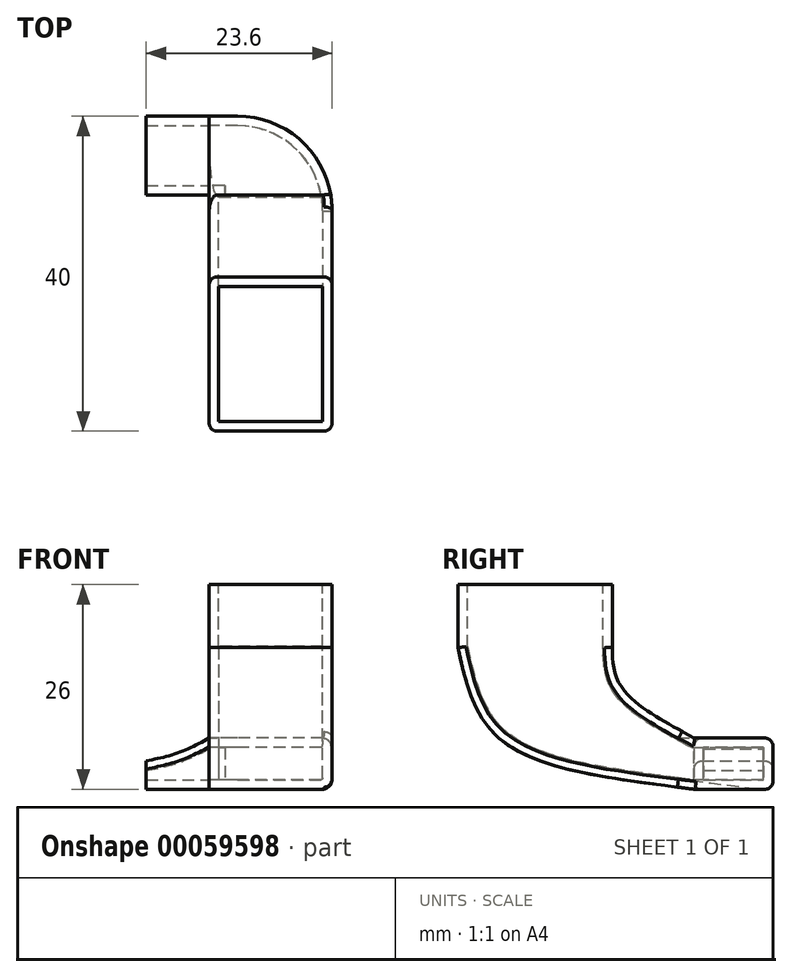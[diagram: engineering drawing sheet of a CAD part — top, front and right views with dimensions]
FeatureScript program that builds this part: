
annotation { "Feature Type Name" : "Feature", "Feature Type Description" : "" }
export const myFeature = defineFeature(function(context is Context, id is Id, definition is map)
    precondition{}
    {
        {
            var Q0;
            Q0=qCreatedBy(makeId("Right.planeOp"),FACE);
            var sketch = newSketch(context, id + "F0", { "sketchPlane" : qUnion([Q0])});
            skLineSegment(sketch, "E0.bottom", {"start": v(-14.31, 9.66) * mm, "end": v(25.69, 9.66) * mm, "construction": true});
            skLineSegment(sketch, "E0.top", {"start": v(-14.31, -16.34) * mm, "end": v(25.69, -16.34) * mm, "construction": true});
            skLineSegment(sketch, "E0.left", {"start": v(-14.31, 9.66) * mm, "end": v(-14.31, -16.34) * mm, "construction": true});
            skLineSegment(sketch, "E0.right", {"start": v(25.69, 9.66) * mm, "end": v(25.69, -16.34) * mm, "construction": true});
            skLineSegment(sketch, "E1", {"start": v(5.69, 9.66) * mm, "end": v(5.69, -16.34) * mm, "construction": true});
            skLineSegment(sketch, "E2", {"start": v(-14.31, -3.34) * mm, "end": v(25.69, -3.34) * mm, "construction": true});
            skLineSegment(sketch, "E3.bottom", {"start": v(-14.31, 9.66) * mm, "end": v(5.69, 9.66) * mm, "construction": true});
            skLineSegment(sketch, "E3.top", {"start": v(-14.31, -3.34) * mm, "end": v(5.69, -3.34) * mm, "construction": true});
            skLineSegment(sketch, "E3.left", {"start": v(-14.31, 9.66) * mm, "end": v(-14.31, -3.34) * mm, "construction": true});
            skLineSegment(sketch, "E3.right", {"start": v(5.69, 9.66) * mm, "end": v(5.69, -3.34) * mm, "construction": true});
            skLineSegment(sketch, "E4.bottom", {"start": v(5.69, -3.34) * mm, "end": v(25.69, -3.34) * mm, "construction": true});
            skLineSegment(sketch, "E4.top", {"start": v(5.69, -16.34) * mm, "end": v(25.69, -16.34) * mm, "construction": true});
            skLineSegment(sketch, "E4.left", {"start": v(5.69, -3.34) * mm, "end": v(5.69, -16.34) * mm, "construction": true});
            skLineSegment(sketch, "E4.right", {"start": v(25.69, -3.34) * mm, "end": v(25.69, -16.34) * mm, "construction": true});
            skLineSegment(sketch, "E5.bottom", {"start": v(25.69, 9.66) * mm, "end": v(5.69, 9.66) * mm, "construction": true});
            skLineSegment(sketch, "E5.top", {"start": v(25.69, -3.34) * mm, "end": v(5.69, -3.34) * mm, "construction": true});
            skLineSegment(sketch, "E5.left", {"start": v(25.69, 9.66) * mm, "end": v(25.69, -3.34) * mm, "construction": true});
            skLineSegment(sketch, "E6.bottom", {"start": v(-14.31, -16.34) * mm, "end": v(5.69, -16.34) * mm, "construction": true});
            skLineSegment(sketch, "E6.left", {"start": v(-14.31, -16.34) * mm, "end": v(-14.31, -3.34) * mm, "construction": true});
            skLineSegment(sketch, "E6.right", {"start": v(5.69, -16.34) * mm, "end": v(5.69, -3.34) * mm, "construction": true});
            skLineSegment(sketch, "E7.bottom", {"start": v(-4.31, 9.66) * mm, "end": v(5.69, 9.66) * mm, "construction": true});
            skLineSegment(sketch, "E7.top", {"start": v(-4.31, -3.34) * mm, "end": v(5.69, -3.34) * mm, "construction": true});
            skLineSegment(sketch, "E7.left", {"start": v(-4.31, 9.66) * mm, "end": v(-4.31, -3.34) * mm, "construction": true});
            skLineSegment(sketch, "E8.bottom", {"start": v(15.69, 9.66) * mm, "end": v(25.69, 9.66) * mm, "construction": true});
            skLineSegment(sketch, "E8.top", {"start": v(15.69, -3.34) * mm, "end": v(25.69, -3.34) * mm, "construction": true});
            skLineSegment(sketch, "E8.left", {"start": v(15.69, 9.66) * mm, "end": v(15.69, -3.34) * mm, "construction": true});
            skLineSegment(sketch, "E9.bottom", {"start": v(25.69, -16.34) * mm, "end": v(15.69, -16.34) * mm, "construction": true});
            skLineSegment(sketch, "E9.top", {"start": v(25.69, -3.34) * mm, "end": v(15.69, -3.34) * mm, "construction": true});
            skLineSegment(sketch, "E9.left", {"start": v(25.69, -16.34) * mm, "end": v(25.69, -3.34) * mm, "construction": true});
            skLineSegment(sketch, "E9.right", {"start": v(15.69, -16.34) * mm, "end": v(15.69, -3.34) * mm, "construction": true});
            skLineSegment(sketch, "E10.bottom", {"start": v(-4.31, -16.34) * mm, "end": v(5.69, -16.34) * mm, "construction": true});
            skLineSegment(sketch, "E10.left", {"start": v(-4.31, -16.34) * mm, "end": v(-4.31, -3.34) * mm, "construction": true});
            skLineSegment(sketch, "E11.bottom", {"start": v(-14.31, 9.66) * mm, "end": v(-4.31, 9.66) * mm, "construction": true});
            skLineSegment(sketch, "E11.top", {"start": v(-14.31, -3.34) * mm, "end": v(-4.31, -3.34) * mm, "construction": true});
            skLineSegment(sketch, "E12.top", {"start": v(-14.31, -16.34) * mm, "end": v(-4.31, -16.34) * mm, "construction": true});
            skLineSegment(sketch, "E12.left", {"start": v(-14.31, -3.34) * mm, "end": v(-14.31, -16.34) * mm, "construction": true});
            skLineSegment(sketch, "E12.right", {"start": v(-4.31, -3.34) * mm, "end": v(-4.31, -16.34) * mm, "construction": true});
            skLineSegment(sketch, "E13.bottom", {"start": v(5.69, 9.66) * mm, "end": v(15.69, 9.66) * mm, "construction": true});
            skLineSegment(sketch, "E13.top", {"start": v(5.69, -3.34) * mm, "end": v(15.69, -3.34) * mm, "construction": true});
            skLineSegment(sketch, "E14.bottom", {"start": v(-14.31, 3.16) * mm, "end": v(25.69, 3.16) * mm, "construction": true});
            skLineSegment(sketch, "E14.left", {"start": v(-14.31, 3.16) * mm, "end": v(-14.31, -3.34) * mm, "construction": true});
            skLineSegment(sketch, "E14.right", {"start": v(25.69, 3.16) * mm, "end": v(25.69, -3.34) * mm, "construction": true});
            skLineSegment(sketch, "E15.top", {"start": v(-14.31, -9.84) * mm, "end": v(25.69, -9.84) * mm, "construction": true});
            skLineSegment(sketch, "E15.left", {"start": v(-14.31, -3.34) * mm, "end": v(-14.31, -9.84) * mm, "construction": true});
            skLineSegment(sketch, "E15.right", {"start": v(25.69, -3.34) * mm, "end": v(25.69, -9.84) * mm, "construction": true});
            skLineSegment(sketch, "E16.bottom", {"start": v(-14.31, 9.66) * mm, "end": v(5.29, 9.66) * mm});
            skLineSegment(sketch, "E16.top", {"start": v(-14.31, 1.66) * mm, "end": v(5.29, 1.66) * mm, "construction": true});
            skLineSegment(sketch, "E16.left", {"start": v(-14.31, 9.66) * mm, "end": v(-14.31, 1.66) * mm});
            skLineSegment(sketch, "E16.right", {"start": v(5.29, 9.66) * mm, "end": v(5.29, 1.66) * mm});
            skLineSegment(sketch, "E17.bottom", {"start": v(25.69, -16.34) * mm, "end": v(15.69, -16.34) * mm});
            skLineSegment(sketch, "E17.top", {"start": v(25.69, -8.34) * mm, "end": v(15.69, -8.34) * mm, "construction": true});
            skLineSegment(sketch, "E17.left", {"start": v(25.69, -16.34) * mm, "end": v(25.69, -8.34) * mm});
            skLineSegment(sketch, "E17.right", {"start": v(15.69, -16.34) * mm, "end": v(15.69, -8.34) * mm, "construction": true});
            skFitSpline(sketch, "E18", {"points": [v(-14.31, 1.66) * mm, v(-9.11, -9.84) * mm, v(15.69, -16.34) * mm], "startDerivative": vector(6.77, -30.78) * mm, "endDerivative": vector(54.04, -6.84) * mm});
            skFitSpline(sketch, "E19", {"points": [v(5.29, 1.66) * mm, v(6.44, -3.34) * mm, v(15.69, -9.84) * mm], "startDerivative": vector(0.34, -12.73) * mm, "endDerivative": vector(19.24, -10.42) * mm});
            skLineSegment(sketch, "E20", {"start": v(15.69, -9.84) * mm, "end": v(25.69, -9.84) * mm});
            skSolve(sketch);
        }
        {
            var Q0;
            Q0=makeQuery(id+"F0.imprint","IMPRINT",FACE,{"disambiguationData":[TD([[makeQuery(id+"F0.imprint","IMPRINT",EDGE,{"derivedFrom":sQuery(id+"F0.wireOp",EDGE,"E16.bottom")}),-1.0]])]});
            var Q1;
            {var subQ4=sQuery(id+"F0.wireOp",EDGE,"E16.top");Q1=makeQuery(id+"F0.imprint","IMPRINT",FACE,{"disambiguationData":[TD([[makeQuery(id+"F0.imprint","IMPRINT",EDGE,{"derivedFrom":subQ4}),-1.0]])]});}
            var Q2;
            {var subQ0=sQuery(id+"F0.wireOp",EDGE,"E17.top");Q2=makeQuery(id+"F0.imprint","IMPRINT",FACE,{"disambiguationData":[TD([[makeQuery(id+"F0.imprint","IMPRINT",EDGE,{"derivedFrom":subQ0}),1.0]])]});}
            extrude(context, id + "F1", {"entities" : qUnion([Q0, Q1, Q2]), "depth" : 15.6 * mm});
        }
        {
            var Q0;
            Q0=makeQuery(id+"F1.opExtrude","SWEPT_FACE",FACE,{"disambiguationData":[OSD([sQuery(id+"F0.wireOp",EDGE,"E17.left")])]});
            cPlane(context, id + "F2", {"entities" : qUnion([Q0]), "cplaneType" : CPlaneType.OFFSET, "offset" : 0 * mm, "width" : 150 * mm, "height" : 150 * mm});
        }
        {
            var Q0;
            Q0=qCreatedBy(id+"F2.planeOp",FACE);
            var sketch = newSketch(context, id + "F3", { "sketchPlane" : qUnion([Q0])});
            skLineSegment(sketch, "E21", {"start": v(-15.6, -12.94) * mm, "end": v(-15.6, -12.74) * mm});
            skLineSegment(sketch, "E22", {"start": v(-15.6, -16.34) * mm, "end": v(-15.6, -9.34) * mm});
            skLineSegment(sketch, "E23.bottom", {"start": v(-15.6, -16.34) * mm, "end": v(-23.6, -16.34) * mm, "construction": true});
            skLineSegment(sketch, "E23.top", {"start": v(-15.6, -9.34) * mm, "end": v(-23.6, -9.34) * mm, "construction": true});
            skLineSegment(sketch, "E23.left", {"start": v(-15.6, -16.34) * mm, "end": v(-15.6, -9.34) * mm, "construction": true});
            skLineSegment(sketch, "E23.right", {"start": v(-23.6, -16.34) * mm, "end": v(-23.6, -9.34) * mm, "construction": true});
            skLineSegment(sketch, "E24.bottom", {"start": v(-13.35, -9.34) * mm, "end": v(-19.6, -9.34) * mm, "construction": true});
            skLineSegment(sketch, "E24.top", {"start": v(-13.35, -16.34) * mm, "end": v(-19.6, -16.34) * mm, "construction": true});
            skLineSegment(sketch, "E24.left", {"start": v(-13.35, -9.34) * mm, "end": v(-13.35, -16.34) * mm, "construction": true});
            skLineSegment(sketch, "E24.right", {"start": v(-19.6, -9.34) * mm, "end": v(-19.6, -16.34) * mm, "construction": true});
            skLineSegment(sketch, "E25.bottom", {"start": v(-19.6, -16.34) * mm, "end": v(-23.6, -16.34) * mm, "construction": true});
            skLineSegment(sketch, "E25.top", {"start": v(-19.6, -9.34) * mm, "end": v(-23.6, -9.34) * mm, "construction": true});
            skLineSegment(sketch, "E25.left", {"start": v(-19.6, -16.34) * mm, "end": v(-19.6, -9.34) * mm, "construction": true});
            skLineSegment(sketch, "E26.bottom", {"start": v(-23.6, -12.84) * mm, "end": v(-19.6, -12.84) * mm, "construction": true});
            skLineSegment(sketch, "E26.top", {"start": v(-23.6, -9.34) * mm, "end": v(-19.6, -9.34) * mm, "construction": true});
            skLineSegment(sketch, "E26.left", {"start": v(-23.6, -12.84) * mm, "end": v(-23.6, -9.34) * mm, "construction": true});
            skLineSegment(sketch, "E26.right", {"start": v(-19.6, -12.84) * mm, "end": v(-19.6, -9.34) * mm, "construction": true});
            skLineSegment(sketch, "E27.bottom", {"start": v(-13.35, -9.34) * mm, "end": v(-23.6, -9.34) * mm, "construction": true});
            skLineSegment(sketch, "E27.top", {"start": v(-13.35, -12.84) * mm, "end": v(-23.6, -12.84) * mm, "construction": true});
            skLineSegment(sketch, "E27.left", {"start": v(-13.35, -9.34) * mm, "end": v(-13.35, -12.84) * mm, "construction": true});
            skLineSegment(sketch, "E27.right", {"start": v(-23.6, -9.34) * mm, "end": v(-23.6, -12.84) * mm, "construction": true});
            skLineSegment(sketch, "E28.bottom", {"start": v(-19.6, -12.84) * mm, "end": v(-15.6, -12.84) * mm, "construction": true});
            skLineSegment(sketch, "E28.top", {"start": v(-19.6, -16.34) * mm, "end": v(-15.6, -16.34) * mm, "construction": true});
            skLineSegment(sketch, "E28.left", {"start": v(-19.6, -12.84) * mm, "end": v(-19.6, -16.34) * mm, "construction": true});
            skLineSegment(sketch, "E28.right", {"start": v(-15.6, -12.84) * mm, "end": v(-15.6, -16.34) * mm, "construction": true});
            skLineSegment(sketch, "E29.bottom", {"start": v(-23.6, -9.34) * mm, "end": v(-21.6, -9.34) * mm, "construction": true});
            skLineSegment(sketch, "E29.top", {"start": v(-23.6, -12.84) * mm, "end": v(-21.6, -12.84) * mm, "construction": true});
            skLineSegment(sketch, "E29.right", {"start": v(-21.6, -9.34) * mm, "end": v(-21.6, -12.84) * mm, "construction": true});
            skLineSegment(sketch, "E30.bottom", {"start": v(-19.6, -12.84) * mm, "end": v(-21.6, -12.84) * mm, "construction": true});
            skLineSegment(sketch, "E30.top", {"start": v(-19.6, -16.34) * mm, "end": v(-21.6, -16.34) * mm, "construction": true});
            skLineSegment(sketch, "E30.right", {"start": v(-21.6, -12.84) * mm, "end": v(-21.6, -16.34) * mm, "construction": true});
            skLineSegment(sketch, "E31.bottom", {"start": v(-19.6, -12.84) * mm, "end": v(-17.6, -12.84) * mm, "construction": true});
            skLineSegment(sketch, "E31.top", {"start": v(-19.6, -16.34) * mm, "end": v(-17.6, -16.34) * mm, "construction": true});
            skLineSegment(sketch, "E31.right", {"start": v(-17.6, -12.84) * mm, "end": v(-17.6, -16.34) * mm, "construction": true});
            skLineSegment(sketch, "E32.bottom", {"start": v(-13.35, -9.34) * mm, "end": v(-17.6, -9.34) * mm, "construction": true});
            skLineSegment(sketch, "E32.top", {"start": v(-13.35, -12.84) * mm, "end": v(-17.6, -12.84) * mm, "construction": true});
            skLineSegment(sketch, "E32.right", {"start": v(-17.6, -9.34) * mm, "end": v(-17.6, -12.84) * mm, "construction": true});
            skLineSegment(sketch, "E33.bottom", {"start": v(-24.97, -16.34) * mm, "end": v(-23.6, -16.34) * mm});
            skLineSegment(sketch, "E33.top", {"start": v(-24.97, -12.74) * mm, "end": v(-23.6, -12.74) * mm, "construction": true});
            skLineSegment(sketch, "E33.left", {"start": v(-23.6, -16.34) * mm, "end": v(-23.6, -12.74) * mm});
            skLineSegment(sketch, "E33.right", {"start": v(-24.97, -16.34) * mm, "end": v(-24.97, -12.74) * mm, "construction": true});
            skLineSegment(sketch, "E34", {"start": v(-15.6, -16.34) * mm, "end": v(-23.6, -16.34) * mm});
            skLineSegment(sketch, "E35", {"start": v(-15.6, -9.84) * mm, "end": v(0, -9.84) * mm});
            skLineSegment(sketch, "E36", {"start": v(-15.6, -16.34) * mm, "end": v(0, -16.34) * mm});
            skLineSegment(sketch, "E37", {"start": v(0, -16.34) * mm, "end": v(0, -9.34) * mm});
            skLineSegment(sketch, "E38", {"start": v(-7.8, -9.84) * mm, "end": v(-7.8, -16.34) * mm, "construction": true});
            skLineSegment(sketch, "E39.MirrorCS", {"start": v(8, -9.34) * mm, "end": v(8, -12.84) * mm, "construction": true});
            skLineSegment(sketch, "E40.MirrorCS", {"start": v(4, -12.84) * mm, "end": v(4, -9.34) * mm, "construction": true});
            skLineSegment(sketch, "E41.MirrorCS", {"start": v(8, -16.34) * mm, "end": v(8, -9.34) * mm, "construction": true});
            skLineSegment(sketch, "E42.MirrorCS", {"start": v(4, -12.84) * mm, "end": v(4, -16.34) * mm, "construction": true});
            skLineSegment(sketch, "E43.MirrorCS", {"start": v(4, -12.84) * mm, "end": v(6, -12.84) * mm, "construction": true});
            skLineSegment(sketch, "E44.MirrorCS", {"start": v(4, -16.34) * mm, "end": v(6, -16.34) * mm, "construction": true});
            skLineSegment(sketch, "E45.MirrorCS", {"start": v(8, -9.34) * mm, "end": v(4, -9.34) * mm, "construction": true});
            skLineSegment(sketch, "E46.MirrorCS", {"start": v(4, -9.34) * mm, "end": v(4, -16.34) * mm, "construction": true});
            skLineSegment(sketch, "E47.MirrorCS", {"start": v(9.37, -12.74) * mm, "end": v(8, -12.74) * mm, "construction": true});
            skLineSegment(sketch, "E48.MirrorCS", {"start": v(8, -12.84) * mm, "end": v(6, -12.84) * mm, "construction": true});
            skLineSegment(sketch, "E49.MirrorCS", {"start": v(4, -16.34) * mm, "end": v(4, -9.34) * mm, "construction": true});
            skLineSegment(sketch, "E50.MirrorCS", {"start": v(2, -9.34) * mm, "end": v(2, -12.84) * mm, "construction": true});
            skLineSegment(sketch, "E51.MirrorCS", {"start": v(6, -12.84) * mm, "end": v(6, -16.34) * mm, "construction": true});
            skLineSegment(sketch, "E52.MirrorCS", {"start": v(2, -12.84) * mm, "end": v(2, -16.34) * mm, "construction": true});
            skLineSegment(sketch, "E53.MirrorCS", {"start": v(6, -9.34) * mm, "end": v(6, -12.84) * mm, "construction": true});
            skLineSegment(sketch, "E54.MirrorCS", {"start": v(8, -16.34) * mm, "end": v(8, -12.74) * mm});
            skLineSegment(sketch, "E55.MirrorCS", {"start": v(4, -12.84) * mm, "end": v(2, -12.84) * mm, "construction": true});
            skLineSegment(sketch, "E56.MirrorCS", {"start": v(4, -9.34) * mm, "end": v(8, -9.34) * mm, "construction": true});
            skLineSegment(sketch, "E57.MirrorCS", {"start": v(4, -16.34) * mm, "end": v(8, -16.34) * mm, "construction": true});
            skLineSegment(sketch, "E58.MirrorCS", {"start": v(9.37, -16.34) * mm, "end": v(8, -16.34) * mm});
            skLineSegment(sketch, "E59.MirrorCS", {"start": v(8, -9.34) * mm, "end": v(6, -9.34) * mm, "construction": true});
            skLineSegment(sketch, "E60.MirrorCS", {"start": v(4, -16.34) * mm, "end": v(2, -16.34) * mm, "construction": true});
            skLineSegment(sketch, "E61.MirrorCS", {"start": v(8, -12.84) * mm, "end": v(4, -12.84) * mm, "construction": true});
            skLineSegment(sketch, "E62.MirrorCS", {"start": v(9.37, -16.34) * mm, "end": v(9.37, -12.74) * mm, "construction": true});
            skLineSegment(sketch, "E63.MirrorCS", {"start": v(8, -12.84) * mm, "end": v(8, -9.34) * mm, "construction": true});
            skLineSegment(sketch, "E64.MirrorCS", {"start": v(0, -12.94) * mm, "end": v(0, -12.74) * mm});
            skLineSegment(sketch, "E65.MirrorCS", {"start": v(-2.25, -9.34) * mm, "end": v(-2.25, -12.84) * mm, "construction": true});
            skLineSegment(sketch, "E66.MirrorCS", {"start": v(0, -12.84) * mm, "end": v(0, -16.34) * mm, "construction": true});
            skLineSegment(sketch, "E67.MirrorCS", {"start": v(0, -16.34) * mm, "end": v(0, -9.34) * mm, "construction": true});
            skLineSegment(sketch, "E68.MirrorCS", {"start": v(-2.25, -9.34) * mm, "end": v(2, -9.34) * mm, "construction": true});
            skLineSegment(sketch, "E69.MirrorCS", {"start": v(-2.25, -9.34) * mm, "end": v(8, -9.34) * mm, "construction": true});
            skLineSegment(sketch, "E70.MirrorCS", {"start": v(0, -16.34) * mm, "end": v(8, -16.34) * mm, "construction": true});
            skLineSegment(sketch, "E71.MirrorCS", {"start": v(-2.25, -16.34) * mm, "end": v(4, -16.34) * mm, "construction": true});
            skLineSegment(sketch, "E72.MirrorCS", {"start": v(-2.25, -9.34) * mm, "end": v(-2.25, -16.34) * mm, "construction": true});
            skLineSegment(sketch, "E73.MirrorCS", {"start": v(0, -9.34) * mm, "end": v(8, -9.34) * mm, "construction": true});
            skLineSegment(sketch, "E74.MirrorCS", {"start": v(4, -12.84) * mm, "end": v(0, -12.84) * mm, "construction": true});
            skLineSegment(sketch, "E75.MirrorCS", {"start": v(4, -16.34) * mm, "end": v(0, -16.34) * mm, "construction": true});
            skLineSegment(sketch, "E76.MirrorCS", {"start": v(-2.25, -9.34) * mm, "end": v(4, -9.34) * mm, "construction": true});
            skLineSegment(sketch, "E77.MirrorCS", {"start": v(0, -16.34) * mm, "end": v(8, -16.34) * mm});
            skLineSegment(sketch, "E78.MirrorCS", {"start": v(-2.25, -12.84) * mm, "end": v(2, -12.84) * mm, "construction": true});
            skLineSegment(sketch, "E79.MirrorCS", {"start": v(-2.25, -12.84) * mm, "end": v(8, -12.84) * mm, "construction": true});
            skFitSpline(sketch, "E80", {"points": [v(-15.6, -9.84) * mm, v(-19.6, -11.79) * mm, v(-23.6, -12.74) * mm], "startDerivative": vector(-7.77, -4.3) * mm, "endDerivative": vector(-8.24, -1.5) * mm});
            skFitSpline(sketch, "E81", {"points": [v(0, -9.84) * mm, v(4, -11.72) * mm, v(8, -12.74) * mm], "startDerivative": vector(7.8, -4.12) * mm, "endDerivative": vector(8.2, -1.67) * mm});
            skSolve(sketch);
        }
        {
            var Q0;
            Q0=makeQuery(id+"F3.imprint","IMPRINT",FACE,{"disambiguationData":[TD([[makeQuery(id+"F3.imprint","IMPRINT",EDGE,{"derivedFrom":sQuery(id+"F3.wireOp",EDGE,"E54.MirrorCS")}),1.0]])]});
            extrude(context, id + "F4", {"entities" : qUnion([Q0]), "oppositeDirection" : true, "depth" : 10 * mm});
        }
        {
            var Q0;
            Q0=makeQuery(id+"F1.opExtrude","CAP_EDGE",EDGE,{"disambiguationData":[OSD([sQuery(id+"F0.wireOp",EDGE,"E17.left")])],"isStart":false});
            fillet(context, id + "F5", {"entities" : qUnion([Q0]), "radius" : 12 * mm, "tangentPropagation" : true, "allowEdgeOverflow" : false});
        }
        {
            var Q0;
            Q0=makeQuery(id+"F1.opExtrude","CAP_FACE",FACE,{"disambiguationData":[OSD([sQuery(id+"F0.wireOp",EDGE,"E16.bottom"),sQuery(id+"F0.wireOp",EDGE,"E16.left"),sQuery(id+"F0.wireOp",EDGE,"E16.right"),sQuery(id+"F0.wireOp",EDGE,"E17.bottom"),sQuery(id+"F0.wireOp",EDGE,"E17.left"),sQuery(id+"F0.wireOp",EDGE,"E18"),sQuery(id+"F0.wireOp",EDGE,"E19"),sQuery(id+"F0.wireOp",EDGE,"E20")])],"isStart":true});
            cPlane(context, id + "F6", {"entities" : qUnion([Q0]), "cplaneType" : CPlaneType.OFFSET, "offset" : 0 * mm, "width" : 150 * mm, "height" : 150 * mm});
        }
        {
            var Q0;
            Q0=qCreatedBy(id+"F6.planeOp",FACE);
            var sketch = newSketch(context, id + "F7", { "sketchPlane" : qUnion([Q0])});
            skPoint(sketch, "E82.0", {"position": v(-25.69, -9.84) * mm});
            skPoint(sketch, "E83.0", {"position": v(-15.69, -9.84) * mm});
            skPoint(sketch, "E84.0", {"position": v(-15.69, -16.34) * mm});
            skPoint(sketch, "E85.0", {"position": v(-25.69, -16.34) * mm});
            skLineSegment(sketch, "E86.bottom", {"start": v(-25.69, -9.84) * mm, "end": v(-15.69, -9.84) * mm});
            skLineSegment(sketch, "E86.top", {"start": v(-25.69, -16.34) * mm, "end": v(-15.69, -16.34) * mm});
            skLineSegment(sketch, "E86.left", {"start": v(-25.69, -9.84) * mm, "end": v(-25.69, -16.34) * mm});
            skLineSegment(sketch, "E86.right", {"start": v(-15.69, -9.84) * mm, "end": v(-15.69, -16.34) * mm});
            skLineSegment(sketch, "E87.0", {"start": v(-24.49, -11.04) * mm, "end": v(-16.89, -11.04) * mm});
            skLineSegment(sketch, "E87.1", {"start": v(-24.49, -11.04) * mm, "end": v(-24.49, -15.14) * mm});
            skLineSegment(sketch, "E87.2", {"start": v(-24.49, -15.14) * mm, "end": v(-16.89, -15.14) * mm});
            skLineSegment(sketch, "E87.3", {"start": v(-16.89, -11.04) * mm, "end": v(-16.89, -15.14) * mm});
            skSolve(sketch);
        }
        {
            var Q0;
            Q0=makeQuery(id+"F7.imprint","IMPRINT",FACE,{"disambiguationData":[TD([[makeQuery(id+"F7.imprint","IMPRINT",EDGE,{"derivedFrom":sQuery(id+"F7.wireOp",EDGE,"E87.0")}),-1.0]])]});
            extrude(context, id + "F8", {"entities" : qUnion([Q0]), "operationType" : NewBodyOperationType.REMOVE, "oppositeDirection" : true, "depth" : 2 * mm});
        }
        {
            var Q0;
            Q0=makeQuery(id+"F4.opExtrude","CAP_EDGE",EDGE,{"disambiguationData":[OSD([sQuery(id+"F3.wireOp",EDGE,"E81")])],"isStart":true});
            var Q1;
            Q1=makeQuery(id+"F4.opExtrude","CAP_EDGE",EDGE,{"disambiguationData":[OSD([sQuery(id+"F3.wireOp",EDGE,"E81")])],"isStart":false});
            var Q2;
            Q2=makeQuery(id+"F4.opExtrude","CAP_EDGE",EDGE,{"disambiguationData":[OSD([sQuery(id+"F3.wireOp",EDGE,"E77.MirrorCS")])],"isStart":false});
            var Q3;
            Q3=makeQuery(id+"F4.opExtrude","CAP_EDGE",EDGE,{"disambiguationData":[OSD([sQuery(id+"F3.wireOp",EDGE,"E77.MirrorCS")])],"isStart":true});
            var Q4;
            Q4=makeQuery(id+"F1.opExtrude","CAP_EDGE",EDGE,{"disambiguationData":[OSD([sQuery(id+"F0.wireOp",EDGE,"E19")])],"isStart":false});
            var Q5;
            Q5=makeQuery(id+"F1.opExtrude","CAP_EDGE",EDGE,{"disambiguationData":[OSD([sQuery(id+"F0.wireOp",EDGE,"E16.right")])],"isStart":false});
            var Q6;
            Q6=makeQuery(id+"F1.opExtrude","CAP_EDGE",EDGE,{"disambiguationData":[OSD([sQuery(id+"F0.wireOp",EDGE,"E18")])],"isStart":false});
            var Q7;
            Q7=makeQuery(id+"F1.opExtrude","CAP_EDGE",EDGE,{"disambiguationData":[OSD([sQuery(id+"F0.wireOp",EDGE,"E16.left")])],"isStart":false});
            var Q8;
            Q8=makeQuery(id+"F1.opExtrude","SWEPT_EDGE",EDGE,{"disambiguationData":[OSD([sQuery(id+"F0.wireOp",EDGE,"E17.left"),sQuery(id+"F0.wireOp",EDGE,"E20")])]});
            var Q9;
            Q9=makeQuery(id+"F1.opExtrude","SWEPT_EDGE",EDGE,{"disambiguationData":[OSD([sQuery(id+"F0.wireOp",EDGE,"E17.bottom"),sQuery(id+"F0.wireOp",EDGE,"E17.left")])]});
            var Q10;
            Q10=makeQuery(id+"F1.opExtrude","CAP_EDGE",EDGE,{"disambiguationData":[OSD([sQuery(id+"F0.wireOp",EDGE,"E19")])],"isStart":true});
            var Q11;
            Q11=makeQuery(id+"F1.opExtrude","CAP_EDGE",EDGE,{"disambiguationData":[OSD([sQuery(id+"F0.wireOp",EDGE,"E16.right")])],"isStart":true});
            var Q12;
            Q12=makeQuery(id+"F1.opExtrude","CAP_EDGE",EDGE,{"disambiguationData":[OSD([sQuery(id+"F0.wireOp",EDGE,"E18")])],"isStart":true});
            var Q13;
            Q13=makeQuery(id+"F1.opExtrude","CAP_EDGE",EDGE,{"disambiguationData":[OSD([sQuery(id+"F0.wireOp",EDGE,"E16.left")])],"isStart":true});
            fillet(context, id + "F9", {"entities" : qUnion([Q0, Q1, Q2, Q3, Q4, Q5, Q6, Q7, Q8, Q9, Q10, Q11, Q12, Q13]), "radius" : 1 * mm, "tangentPropagation" : true, "allowEdgeOverflow" : false});
        }
        {
            var Q0;
            Q0=makeQuery(id+"F1.opExtrude","SWEPT_FACE",FACE,{"disambiguationData":[OSD([sQuery(id+"F0.wireOp",EDGE,"E16.bottom")])]});
            var Q1;
            Q1=makeQuery(id+"F4.opExtrude","SWEPT_FACE",FACE,{"disambiguationData":[OSD([sQuery(id+"F3.wireOp",EDGE,"E54.MirrorCS")])]});
            var Q2;
            Q2=makeQuery(id+"F4.opExtrude","SWEPT_FACE",FACE,{"disambiguationData":[OSD([sQuery(id+"F3.wireOp",EDGE,"E37")])]});
            var Q3;
            Q3=makeQuery(id+"F8.opExtrude","CAP_FACE",FACE,{"disambiguationData":[OSD([sQuery(id+"F7.wireOp",EDGE,"E86.bottom"),sQuery(id+"F7.wireOp",EDGE,"E86.top"),sQuery(id+"F7.wireOp",EDGE,"E86.left"),sQuery(id+"F7.wireOp",EDGE,"E86.right")])],"isStart":true});
            var Q4;
            Q4=makeQuery(id+"F8.opExtrude","CAP_FACE",FACE,{"disambiguationData":[OSD([sQuery(id+"F7.wireOp",EDGE,"E86.bottom"),sQuery(id+"F7.wireOp",EDGE,"E86.top"),sQuery(id+"F7.wireOp",EDGE,"E86.left"),sQuery(id+"F7.wireOp",EDGE,"E86.right")])],"isStart":false});
            var Q5;
            Q5=makeQuery(id+"F8.boolean.opBoolean","COPY",FACE,{"derivedFrom":makeQuery(id+"F8.opExtrude","CAP_FACE",FACE,{"disambiguationData":[OSD([sQuery(id+"F7.wireOp",EDGE,"E87.0"),sQuery(id+"F7.wireOp",EDGE,"E87.1"),sQuery(id+"F7.wireOp",EDGE,"E87.2"),sQuery(id+"F7.wireOp",EDGE,"E87.3")])],"isStart":false})});
            var Q6;
            Q6=makeQuery(id+"F1.opExtrude","SWEPT_BODY",BODY,{"disambiguationData":[OSD([sQuery(id+"F0.wireOp",EDGE,"E16.bottom"),sQuery(id+"F0.wireOp",EDGE,"E16.left"),sQuery(id+"F0.wireOp",EDGE,"E16.right"),sQuery(id+"F0.wireOp",EDGE,"E17.bottom"),sQuery(id+"F0.wireOp",EDGE,"E17.left"),sQuery(id+"F0.wireOp",EDGE,"E18"),sQuery(id+"F0.wireOp",EDGE,"E19"),sQuery(id+"F0.wireOp",EDGE,"E20")])]});
            shell(context, id + "F10", {"entities" : qUnion([Q0, Q1, Q2, Q3, Q4, Q5]), "parts" : qUnion([Q6]), "thickness" : 1.2 * mm});
        }
    });
